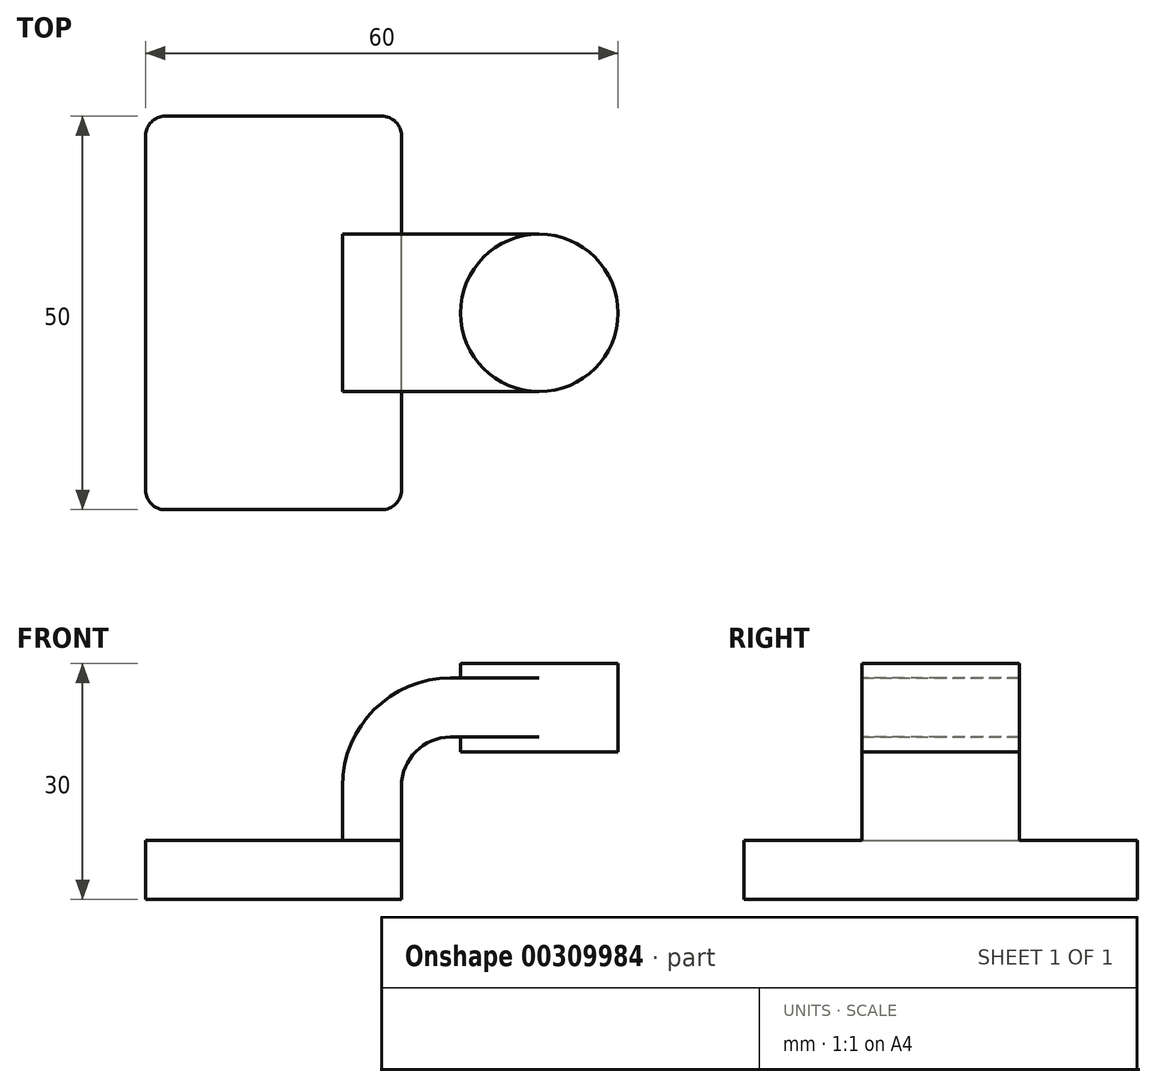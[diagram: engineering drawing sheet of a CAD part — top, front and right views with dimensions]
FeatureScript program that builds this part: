
annotation { "Feature Type Name" : "Feature", "Feature Type Description" : "" }
export const myFeature = defineFeature(function(context is Context, id is Id, definition is map)
    precondition{}
    {
        {
            var Q0;
            Q0=qCreatedBy(makeId("Front.planeOp"),FACE);
            var sketch = newSketch(context, id + "F0", { "sketchPlane" : qUnion([Q0])});
            skLineSegment(sketch, "E0.bottom", {"start": v(16.25, 3.75) * mm, "end": v(-16.25, 3.75) * mm});
            skLineSegment(sketch, "E0.top", {"start": v(16.25, -3.75) * mm, "end": v(-16.25, -3.75) * mm});
            skLineSegment(sketch, "E0.left", {"start": v(16.25, 3.75) * mm, "end": v(16.25, -3.75) * mm});
            skLineSegment(sketch, "E0.right", {"start": v(-16.25, 3.75) * mm, "end": v(-16.25, -3.75) * mm});
            skPoint(sketch, "E0.middle", {"position": v(0, 0) * mm});
            skLineSegment(sketch, "E1.bottom", {"start": v(43.75, 15) * mm, "end": v(23.75, 15) * mm});
            skLineSegment(sketch, "E1.top", {"start": v(43.75, 26.25) * mm, "end": v(23.75, 26.25) * mm});
            skLineSegment(sketch, "E1.left", {"start": v(43.75, 15) * mm, "end": v(43.75, 26.25) * mm});
            skLineSegment(sketch, "E1.right", {"start": v(23.75, 15) * mm, "end": v(23.75, 26.25) * mm});
            skPoint(sketch, "E1.middle", {"position": v(33.75, 20.63) * mm});
            skLineSegment(sketch, "E2", {"start": v(16.25, 3.75) * mm, "end": v(16.25, 10.63) * mm});
            skArc(sketch, "E3", {"start": v(16.25, 10.63) * mm, "mid": v(18.08, 15.04) * mm, "end": v(22.5, 16.88) * mm});
            skLineSegment(sketch, "E4", {"start": v(22.5, 16.88) * mm, "end": v(33.75, 16.88) * mm});
            skLineSegment(sketch, "E5.0", {"start": v(22.5, 24.38) * mm, "end": v(33.75, 24.38) * mm});
            skArc(sketch, "E5.1", {"start": v(8.75, 10.63) * mm, "mid": v(12.78, 20.35) * mm, "end": v(22.5, 24.38) * mm});
            skLineSegment(sketch, "E5.2", {"start": v(8.75, 3.75) * mm, "end": v(8.75, 10.63) * mm});
            skFitSpline(sketch, "E6", {"points": [v(-16.25, 3.75) * mm, v(22.5, 24.38) * mm], "startDerivative": vector(0, 41.4) * mm, "endDerivative": vector(54.03, 0) * mm});
            skLineSegment(sketch, "E7", {"start": v(33.75, 15) * mm, "end": v(33.75, 26.25) * mm});
            skSolve(sketch);
        }
        {
            var Q0;
            Q0=makeQuery(id+"F0.imprint","IMPRINT",FACE,{"disambiguationData":[TD([[makeQuery(id+"F0.imprint","IMPRINT",EDGE,{"derivedFrom":sQuery(id+"F0.wireOp",EDGE,"E0.top")}),-1.0]])]});
            extrude(context, id + "F1", {"entities" : qUnion([Q0]), "depth" : 50 * mm, "symmetric" : true});
        }
        {
            var Q0;
            {var subQ1=sQuery(id+"F0.wireOp",EDGE,"E2");Q0=makeQuery(id+"F0.imprint","IMPRINT",FACE,{"disambiguationData":[TD([[makeQuery(id+"F0.imprint","IMPRINT",EDGE,{"derivedFrom":subQ1}),1.0]])]});}
            var Q1;
            {var subQ0=sQuery(id+"F0.wireOp",EDGE,"E4");var subQ1=sQuery(id+"F0.wireOp",EDGE,"E1.right");var subQ2=makeQuery(id+"F0.imprint","INTERSECT",VERTEX,{"derivedFrom":[subQ1,subQ0]});Q1=makeQuery(id+"F0.imprint","IMPRINT",FACE,{"disambiguationData":[TD([[makeQuery(id+"F0.imprint","IMPRINT",EDGE,{"disambiguationData":[TD([[subQ2,-1.0]])],"derivedFrom":subQ1}),-1.0]])]});}
            extrude(context, id + "F2", {"entities" : qUnion([Q0, Q1]), "operationType" : NewBodyOperationType.ADD, "depth" : 20 * mm, "symmetric" : true});
        }
        {
            var Q0;
            Q0=makeQuery(id+"F0.imprint","IMPRINT",FACE,{"disambiguationData":[TD([[makeQuery(id+"F0.imprint","IMPRINT",EDGE,{"derivedFrom":sQuery(id+"F0.wireOp",EDGE,"E5.1")}),1.0]])]});
            extrude(context, id + "F3", {"entities" : qUnion([Q0]), "operationType" : NewBodyOperationType.ADD, "depth" : 6.25 * mm, "symmetric" : true});
        }
        {
            var Q0;
            {var subQ0=sQuery(id+"F0.wireOp",EDGE,"E1.left");Q0=makeQuery(id+"F0.imprint","IMPRINT",FACE,{"disambiguationData":[TD([[makeQuery(id+"F0.imprint","IMPRINT",EDGE,{"derivedFrom":subQ0}),1.0]])]});}
            var Q1;
            Q1=sQuery(id+"F0.wireOp",EDGE,"E7");
            revolve(context, id + "F4", {"operationType" : NewBodyOperationType.ADD, "entities" : qUnion([Q0]), "axis" : qUnion([Q1]), "revolveType" : RevolveType.FULL});
        }
        {
            var Q0;
            Q0=makeQuery(id+"F1.opExtrude","CAP_EDGE",EDGE,{"disambiguationData":[OSD([sQuery(id+"F0.wireOp",EDGE,"E0.left")])],"isStart":false});
            var Q1;
            Q1=makeQuery(id+"F1.opExtrude","CAP_EDGE",EDGE,{"disambiguationData":[OSD([sQuery(id+"F0.wireOp",EDGE,"E0.right")])],"isStart":false});
            var Q2;
            Q2=makeQuery(id+"F1.opExtrude","CAP_EDGE",EDGE,{"disambiguationData":[OSD([sQuery(id+"F0.wireOp",EDGE,"E0.left")])],"isStart":true});
            var Q3;
            Q3=makeQuery(id+"F1.opExtrude","CAP_EDGE",EDGE,{"disambiguationData":[OSD([sQuery(id+"F0.wireOp",EDGE,"E0.right")])],"isStart":true});
            fillet(context, id + "F5", {"entities" : qUnion([Q0, Q1, Q2, Q3]), "radius" : 2.5 * mm, "tangentPropagation" : true, "allowEdgeOverflow" : false});
        }
    });
